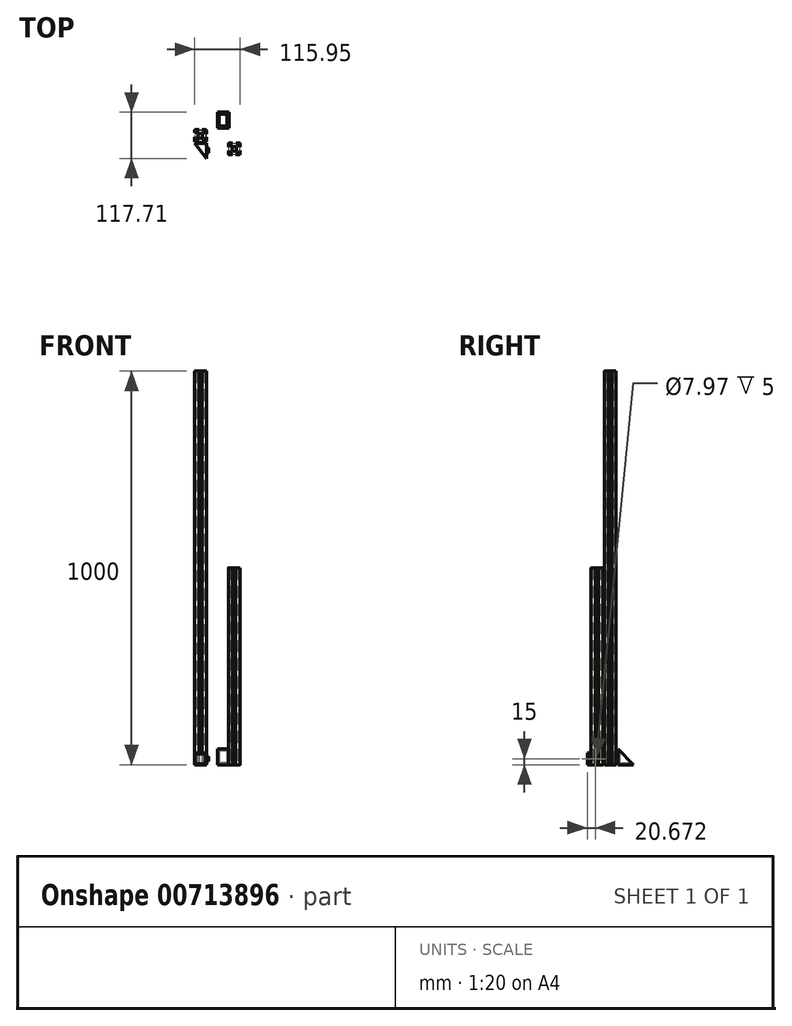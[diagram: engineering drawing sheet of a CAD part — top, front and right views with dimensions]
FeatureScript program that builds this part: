
annotation { "Feature Type Name" : "Feature", "Feature Type Description" : "" }
export const myFeature = defineFeature(function(context is Context, id is Id, definition is map)
    precondition{}
    {
        {
            var Q0;
            Q0=qCreatedBy(makeId("Top.planeOp"),FACE);
            var sketch = newSketch(context, id + "F0", { "sketchPlane" : qUnion([Q0])});
            skPoint(sketch, "E0.middle", {"position": v(-42.85, -16.21) * mm});
            skLineSegment(sketch, "E1.bottom", {"start": v(-36.85, -22.2) * mm, "end": v(-48.85, -22.2) * mm});
            skLineSegment(sketch, "E1.top", {"start": v(-36.85, -10.21) * mm, "end": v(-48.85, -10.21) * mm});
            skLineSegment(sketch, "E1.left", {"start": v(-36.85, -22.2) * mm, "end": v(-36.85, -10.21) * mm});
            skLineSegment(sketch, "E1.right", {"start": v(-48.85, -22.2) * mm, "end": v(-48.85, -10.21) * mm});
            skLineSegment(sketch, "E2.bottom", {"start": v(-51.1, -1.2) * mm, "end": v(-55.85, -1.2) * mm});
            skLineSegment(sketch, "E2.top", {"start": v(-51.1, -7.95) * mm, "end": v(-57.85, -7.95) * mm});
            skLineSegment(sketch, "E2.left", {"start": v(-51.1, -1.2) * mm, "end": v(-51.1, -7.95) * mm});
            skLineSegment(sketch, "E2.right", {"start": v(-57.85, -3.2) * mm, "end": v(-57.85, -7.95) * mm});
            skPoint(sketch, "E2.middle", {"position": v(-54.47, -4.58) * mm});
            skLineSegment(sketch, "E3", {"start": v(-51.1, -1.2) * mm, "end": v(-46.85, -1.2) * mm});
            skLineSegment(sketch, "E4", {"start": v(-46.85, -1.2) * mm, "end": v(-46.85, -3.2) * mm});
            skLineSegment(sketch, "E5", {"start": v(-46.85, -3.2) * mm, "end": v(-51.1, -3.2) * mm});
            skLineSegment(sketch, "E6.bottom", {"start": v(-57.85, -7.95) * mm, "end": v(-55.85, -7.95) * mm});
            skLineSegment(sketch, "E6.top", {"start": v(-57.85, -12.2) * mm, "end": v(-55.85, -12.2) * mm});
            skLineSegment(sketch, "E6.left", {"start": v(-57.85, -7.95) * mm, "end": v(-57.85, -12.2) * mm});
            skLineSegment(sketch, "E6.right", {"start": v(-55.85, -7.95) * mm, "end": v(-55.85, -12.2) * mm});
            skPoint(sketch, "E7", {"position": v(-57.85, -7.95) * mm});
            skPoint(sketch, "E8.visualSharp", {"position": v(-57.85, -1.2) * mm});
            skArc(sketch, "E8.filletArc", {"start": v(-55.85, -1.2) * mm, "mid": v(-57.26, -1.79) * mm, "end": v(-57.85, -3.2) * mm});
            skLineSegment(sketch, "E9", {"start": v(-51.1, -6.76) * mm, "end": v(-47.77, -10.21) * mm});
            skLineSegment(sketch, "E10", {"start": v(-47.77, -10.21) * mm, "end": v(-49.3, -8.63) * mm});
            skLineSegment(sketch, "E11", {"start": v(-52.34, -7.95) * mm, "end": v(-48.85, -11.52) * mm});
            skLineSegment(sketch, "E12.1.0.0", {"start": v(-27.8, -12.2) * mm, "end": v(-29.8, -12.2) * mm});
            skPoint(sketch, "E12.1.0.1", {"position": v(-34.55, -1.2) * mm});
            skLineSegment(sketch, "E12.1.0.2", {"start": v(-27.8, -7.95) * mm, "end": v(-34.55, -7.95) * mm});
            skLineSegment(sketch, "E12.1.0.3", {"start": v(-27.8, -7.95) * mm, "end": v(-27.8, -12.2) * mm});
            skArc(sketch, "E12.1.0.4", {"start": v(-27.8, -3.2) * mm, "mid": v(-28.39, -1.79) * mm, "end": v(-29.8, -1.2) * mm});
            skPoint(sketch, "E12.1.0.5", {"position": v(-27.8, -1.2) * mm});
            skPoint(sketch, "E12.1.0.6", {"position": v(-31.18, -4.57) * mm});
            skLineSegment(sketch, "E12.1.0.7", {"start": v(-34.55, -1.2) * mm, "end": v(-34.55, -3.2) * mm});
            skLineSegment(sketch, "E12.1.0.8", {"start": v(-33.29, -7.95) * mm, "end": v(-36.85, -11.37) * mm});
            skLineSegment(sketch, "E12.1.0.9", {"start": v(-29.8, -12.2) * mm, "end": v(-29.8, -7.95) * mm});
            skLineSegment(sketch, "E12.1.0.10", {"start": v(-29.8, -1.2) * mm, "end": v(-34.55, -1.2) * mm});
            skLineSegment(sketch, "E12.1.0.11", {"start": v(-34.55, -7.95) * mm, "end": v(-34.55, -1.2) * mm});
            skLineSegment(sketch, "E12.1.0.12", {"start": v(-27.8, -7.95) * mm, "end": v(-27.8, -3.2) * mm});
            skLineSegment(sketch, "E12.1.0.13", {"start": v(-34.55, -6.7) * mm, "end": v(-38.14, -10.21) * mm});
            skLineSegment(sketch, "E12.1.0.15", {"start": v(-34.55, -3.2) * mm, "end": v(-38.8, -3.2) * mm});
            skLineSegment(sketch, "E12.1.0.16", {"start": v(-34.55, -1.2) * mm, "end": v(-38.8, -1.2) * mm});
            skLineSegment(sketch, "E12.1.0.17", {"start": v(-38.8, -1.2) * mm, "end": v(-38.8, -3.2) * mm});
            skPoint(sketch, "E13.1.0.0", {"position": v(-27.86, -24.46) * mm});
            skLineSegment(sketch, "E13.1.0.1", {"start": v(-27.86, -29.2) * mm, "end": v(-27.86, -24.46) * mm});
            skLineSegment(sketch, "E13.1.0.2", {"start": v(-27.86, -20.2) * mm, "end": v(-29.86, -20.2) * mm});
            skLineSegment(sketch, "E13.1.0.3", {"start": v(-27.86, -24.46) * mm, "end": v(-27.86, -20.2) * mm});
            skLineSegment(sketch, "E13.1.0.4", {"start": v(-27.86, -24.46) * mm, "end": v(-29.86, -24.46) * mm});
            skLineSegment(sketch, "E13.1.0.5", {"start": v(-34.6, -31.2) * mm, "end": v(-34.6, -24.46) * mm});
            skLineSegment(sketch, "E13.1.0.6", {"start": v(-33.36, -24.46) * mm, "end": v(-36.85, -20.89) * mm});
            skPoint(sketch, "E13.1.0.7", {"position": v(-27.86, -31.2) * mm});
            skLineSegment(sketch, "E13.1.0.8", {"start": v(-34.6, -24.46) * mm, "end": v(-27.86, -24.46) * mm});
            skPoint(sketch, "E13.1.0.9", {"position": v(-31.23, -27.83) * mm});
            skLineSegment(sketch, "E13.1.0.10", {"start": v(-34.6, -31.2) * mm, "end": v(-29.86, -31.2) * mm});
            skLineSegment(sketch, "E13.1.0.11", {"start": v(-29.86, -24.46) * mm, "end": v(-29.86, -20.2) * mm});
            skArc(sketch, "E13.1.0.12", {"start": v(-29.86, -31.2) * mm, "mid": v(-28.44, -30.62) * mm, "end": v(-27.86, -29.2) * mm});
            skLineSegment(sketch, "E13.1.0.13", {"start": v(-34.6, -25.65) * mm, "end": v(-37.93, -22.2) * mm});
            skLineSegment(sketch, "E13.1.0.14", {"start": v(-38.86, -29.2) * mm, "end": v(-34.6, -29.2) * mm});
            skLineSegment(sketch, "E13.1.0.15", {"start": v(-34.6, -31.2) * mm, "end": v(-38.86, -31.2) * mm});
            skLineSegment(sketch, "E13.1.0.16", {"start": v(-38.86, -31.2) * mm, "end": v(-38.86, -29.2) * mm});
            skPoint(sketch, "E14.1.0.0", {"position": v(-51.08, -31.19) * mm});
            skLineSegment(sketch, "E14.1.0.1", {"start": v(-55.83, -31.19) * mm, "end": v(-51.08, -31.19) * mm});
            skLineSegment(sketch, "E14.1.0.2", {"start": v(-46.83, -31.19) * mm, "end": v(-46.83, -29.19) * mm});
            skLineSegment(sketch, "E14.1.0.3", {"start": v(-51.08, -31.19) * mm, "end": v(-46.83, -31.19) * mm});
            skLineSegment(sketch, "E14.1.0.4", {"start": v(-51.08, -31.19) * mm, "end": v(-51.08, -29.19) * mm});
            skLineSegment(sketch, "E14.1.0.5", {"start": v(-57.83, -24.44) * mm, "end": v(-51.08, -24.44) * mm});
            skLineSegment(sketch, "E14.1.0.6", {"start": v(-51.08, -25.68) * mm, "end": v(-47.51, -22.2) * mm});
            skPoint(sketch, "E14.1.0.7", {"position": v(-57.83, -31.19) * mm});
            skLineSegment(sketch, "E14.1.0.8", {"start": v(-51.08, -24.44) * mm, "end": v(-51.08, -31.19) * mm});
            skPoint(sketch, "E14.1.0.9", {"position": v(-54.45, -27.81) * mm});
            skLineSegment(sketch, "E14.1.0.10", {"start": v(-57.83, -24.44) * mm, "end": v(-57.83, -29.19) * mm});
            skLineSegment(sketch, "E14.1.0.11", {"start": v(-51.08, -29.19) * mm, "end": v(-46.83, -29.19) * mm});
            skArc(sketch, "E14.1.0.12", {"start": v(-57.83, -29.19) * mm, "mid": v(-57.24, -30.6) * mm, "end": v(-55.83, -31.19) * mm});
            skLineSegment(sketch, "E14.1.0.13", {"start": v(-52.28, -24.44) * mm, "end": v(-48.82, -21.12) * mm});
            skLineSegment(sketch, "E14.1.0.14", {"start": v(-55.83, -20.19) * mm, "end": v(-55.83, -24.44) * mm});
            skLineSegment(sketch, "E14.1.0.15", {"start": v(-57.83, -24.44) * mm, "end": v(-57.83, -20.19) * mm});
            skLineSegment(sketch, "E14.1.0.16", {"start": v(-57.83, -20.19) * mm, "end": v(-55.83, -20.19) * mm});
            skSolve(sketch);
        }
        {
            var Q0;
            {var subQ1=sQuery(id+"F0.wireOp",EDGE,"E1.bottom");var subQ4=sQuery(id+"F0.wireOp",EDGE,"E1.left");var subQ9=makeQuery(id+"F0.imprint","INTERSECT",VERTEX,{"derivedFrom":[subQ1,subQ4]});Q0=makeQuery(id+"F0.imprint","IMPRINT",FACE,{"disambiguationData":[TD([[makeQuery(id+"F0.imprint","IMPRINT",EDGE,{"disambiguationData":[TD([[subQ9,-1.0]])],"derivedFrom":subQ1}),-1.0]])]});}
            var Q1;
            {var subQ6=sQuery(id+"F0.wireOp",EDGE,"E14.1.0.1");Q1=makeQuery(id+"F0.imprint","IMPRINT",FACE,{"disambiguationData":[TD([[makeQuery(id+"F0.imprint","IMPRINT",EDGE,{"derivedFrom":subQ6}),1.0]])]});}
            var Q2;
            Q2=makeQuery(id+"F0.imprint","IMPRINT",FACE,{"disambiguationData":[TD([[makeQuery(id+"F0.imprint","IMPRINT",EDGE,{"derivedFrom":sQuery(id+"F0.wireOp",EDGE,"E12.1.0.4")}),1.0]])]});
            var Q3;
            {var subQ6=sQuery(id+"F0.wireOp",EDGE,"E13.1.0.1");Q3=makeQuery(id+"F0.imprint","IMPRINT",FACE,{"disambiguationData":[TD([[makeQuery(id+"F0.imprint","IMPRINT",EDGE,{"derivedFrom":subQ6}),1.0]])]});}
            var Q4;
            {var subQ1=sQuery(id+"F0.wireOp",EDGE,"E2.bottom");Q4=makeQuery(id+"F0.imprint","IMPRINT",FACE,{"disambiguationData":[TD([[makeQuery(id+"F0.imprint","IMPRINT",EDGE,{"derivedFrom":subQ1}),1.0]])]});}
            var Q5;
            {var subQ0=sQuery(id+"F0.wireOp",EDGE,"E3");Q5=makeQuery(id+"F0.imprint","IMPRINT",FACE,{"disambiguationData":[TD([[makeQuery(id+"F0.imprint","IMPRINT",EDGE,{"derivedFrom":subQ0}),-1.0]])]});}
            var Q6;
            Q6=makeQuery(id+"F0.imprint","IMPRINT",FACE,{"disambiguationData":[TD([[makeQuery(id+"F0.imprint","IMPRINT",EDGE,{"derivedFrom":sQuery(id+"F0.wireOp",EDGE,"E6.bottom")}),-1.0]])]});
            var Q7;
            Q7=makeQuery(id+"F0.imprint","IMPRINT",FACE,{"disambiguationData":[TD([[makeQuery(id+"F0.imprint","IMPRINT",EDGE,{"derivedFrom":sQuery(id+"F0.wireOp",EDGE,"E12.1.0.0")}),-1.0]])]});
            var Q8;
            Q8=makeQuery(id+"F0.imprint","IMPRINT",FACE,{"disambiguationData":[TD([[makeQuery(id+"F0.imprint","IMPRINT",EDGE,{"derivedFrom":sQuery(id+"F0.wireOp",EDGE,"E13.1.0.2")}),1.0]])]});
            var Q9;
            Q9=makeQuery(id+"F0.imprint","IMPRINT",FACE,{"disambiguationData":[TD([[makeQuery(id+"F0.imprint","IMPRINT",EDGE,{"derivedFrom":sQuery(id+"F0.wireOp",EDGE,"E14.1.0.2")}),1.0]])]});
            var Q10;
            {var subQ2=sQuery(id+"F0.wireOp",EDGE,"E14.1.0.14");Q10=makeQuery(id+"F0.imprint","IMPRINT",FACE,{"disambiguationData":[TD([[makeQuery(id+"F0.imprint","IMPRINT",EDGE,{"derivedFrom":subQ2}),-1.0]])]});}
            var Q11;
            {var subQ0=sQuery(id+"F0.wireOp",EDGE,"E13.1.0.6");Q11=makeQuery(id+"F0.imprint","IMPRINT",FACE,{"disambiguationData":[TD([[makeQuery(id+"F0.imprint","IMPRINT",EDGE,{"derivedFrom":subQ0}),1.0]])]});}
            var Q12;
            {var subQ3=sQuery(id+"F0.wireOp",EDGE,"E1.bottom");var subQ9=sQuery(id+"F0.wireOp",EDGE,"E1.right");var subQ10=makeQuery(id+"F0.imprint","INTERSECT",VERTEX,{"derivedFrom":[subQ3,subQ9]});Q12=makeQuery(id+"F0.imprint","IMPRINT",FACE,{"disambiguationData":[TD([[makeQuery(id+"F0.imprint","IMPRINT",EDGE,{"disambiguationData":[TD([[subQ10,1.0]])],"derivedFrom":subQ3}),1.0]])]});}
            var Q13;
            {var subQ0=sQuery(id+"F0.wireOp",EDGE,"E12.1.0.8");Q13=makeQuery(id+"F0.imprint","IMPRINT",FACE,{"disambiguationData":[TD([[makeQuery(id+"F0.imprint","IMPRINT",EDGE,{"derivedFrom":subQ0}),-1.0]])]});}
            var Q14;
            {var subQ3=sQuery(id+"F0.wireOp",EDGE,"E9");Q14=makeQuery(id+"F0.imprint","IMPRINT",FACE,{"disambiguationData":[TD([[makeQuery(id+"F0.imprint","IMPRINT",EDGE,{"derivedFrom":subQ3}),-1.0]])]});}
            var Q15;
            {var subQ2=sQuery(id+"F0.wireOp",EDGE,"E12.1.0.15");Q15=makeQuery(id+"F0.imprint","IMPRINT",FACE,{"disambiguationData":[TD([[makeQuery(id+"F0.imprint","IMPRINT",EDGE,{"derivedFrom":subQ2}),-1.0]])]});}
            var Q16;
            {var subQ2=sQuery(id+"F0.wireOp",EDGE,"E13.1.0.14");Q16=makeQuery(id+"F0.imprint","IMPRINT",FACE,{"disambiguationData":[TD([[makeQuery(id+"F0.imprint","IMPRINT",EDGE,{"derivedFrom":subQ2}),-1.0]])]});}
            extrude(context, id + "F1", {"entities" : qUnion([Q0, Q1, Q2, Q3, Q4, Q5, Q6, Q7, Q8, Q9, Q10, Q11, Q12, Q13, Q14, Q15, Q16]), "depth" : 1000 * mm, "offsetDistance" : 25 * mm});
        }
        {
            var Q0;
            Q0=qCreatedBy(makeId("Top.planeOp"),FACE);
            var sketch = newSketch(context, id + "F2", { "sketchPlane" : qUnion([Q0])});
            skPoint(sketch, "E15.middle", {"position": v(42.98, -49.46) * mm});
            skLineSegment(sketch, "E16.bottom", {"start": v(48.98, -55.46) * mm, "end": v(36.98, -55.46) * mm});
            skLineSegment(sketch, "E16.top", {"start": v(48.98, -43.46) * mm, "end": v(36.98, -43.46) * mm});
            skLineSegment(sketch, "E16.left", {"start": v(48.98, -55.46) * mm, "end": v(48.98, -43.46) * mm});
            skLineSegment(sketch, "E16.right", {"start": v(36.98, -55.46) * mm, "end": v(36.98, -43.46) * mm});
            skLineSegment(sketch, "E17.bottom", {"start": v(34.73, -34.45) * mm, "end": v(29.98, -34.45) * mm});
            skLineSegment(sketch, "E17.top", {"start": v(34.73, -41.2) * mm, "end": v(27.98, -41.2) * mm});
            skLineSegment(sketch, "E17.left", {"start": v(34.73, -34.45) * mm, "end": v(34.73, -41.2) * mm});
            skLineSegment(sketch, "E17.right", {"start": v(27.98, -36.45) * mm, "end": v(27.98, -41.2) * mm});
            skPoint(sketch, "E17.middle", {"position": v(31.35, -37.83) * mm});
            skLineSegment(sketch, "E18", {"start": v(34.73, -34.45) * mm, "end": v(38.98, -34.45) * mm});
            skLineSegment(sketch, "E19", {"start": v(38.98, -34.45) * mm, "end": v(38.98, -36.45) * mm});
            skLineSegment(sketch, "E20", {"start": v(38.98, -36.45) * mm, "end": v(34.73, -36.45) * mm});
            skLineSegment(sketch, "E21.bottom", {"start": v(27.98, -41.2) * mm, "end": v(29.98, -41.2) * mm});
            skLineSegment(sketch, "E21.top", {"start": v(27.98, -45.45) * mm, "end": v(29.98, -45.45) * mm});
            skLineSegment(sketch, "E21.left", {"start": v(27.98, -41.2) * mm, "end": v(27.98, -45.45) * mm});
            skLineSegment(sketch, "E21.right", {"start": v(29.98, -41.2) * mm, "end": v(29.98, -45.45) * mm});
            skPoint(sketch, "E22", {"position": v(27.98, -41.2) * mm});
            skPoint(sketch, "E23.visualSharp", {"position": v(27.98, -34.45) * mm});
            skArc(sketch, "E23.filletArc", {"start": v(29.98, -34.45) * mm, "mid": v(28.57, -35.04) * mm, "end": v(27.98, -36.45) * mm});
            skLineSegment(sketch, "E24", {"start": v(34.73, -40) * mm, "end": v(38.06, -43.46) * mm});
            skLineSegment(sketch, "E25", {"start": v(38.06, -43.46) * mm, "end": v(36.53, -41.88) * mm});
            skLineSegment(sketch, "E26", {"start": v(33.49, -41.2) * mm, "end": v(36.98, -44.77) * mm});
            skLineSegment(sketch, "E27.1.0.0", {"start": v(58.03, -45.45) * mm, "end": v(56.03, -45.45) * mm});
            skPoint(sketch, "E27.1.0.1", {"position": v(51.28, -34.45) * mm});
            skLineSegment(sketch, "E27.1.0.2", {"start": v(58.03, -41.2) * mm, "end": v(51.28, -41.2) * mm});
            skLineSegment(sketch, "E27.1.0.3", {"start": v(58.03, -41.2) * mm, "end": v(58.03, -45.45) * mm});
            skArc(sketch, "E27.1.0.4", {"start": v(58.03, -36.45) * mm, "mid": v(57.44, -35.04) * mm, "end": v(56.03, -34.45) * mm});
            skPoint(sketch, "E27.1.0.5", {"position": v(58.03, -34.45) * mm});
            skPoint(sketch, "E27.1.0.6", {"position": v(54.65, -37.82) * mm});
            skLineSegment(sketch, "E27.1.0.7", {"start": v(51.28, -34.45) * mm, "end": v(51.28, -36.45) * mm});
            skLineSegment(sketch, "E27.1.0.8", {"start": v(52.54, -41.2) * mm, "end": v(48.98, -44.62) * mm});
            skLineSegment(sketch, "E27.1.0.9", {"start": v(56.03, -45.45) * mm, "end": v(56.03, -41.2) * mm});
            skLineSegment(sketch, "E27.1.0.10", {"start": v(56.03, -34.45) * mm, "end": v(51.28, -34.45) * mm});
            skLineSegment(sketch, "E27.1.0.11", {"start": v(51.28, -41.2) * mm, "end": v(51.28, -34.45) * mm});
            skLineSegment(sketch, "E27.1.0.12", {"start": v(58.03, -41.2) * mm, "end": v(58.03, -36.45) * mm});
            skLineSegment(sketch, "E27.1.0.13", {"start": v(51.28, -39.96) * mm, "end": v(47.7, -43.46) * mm});
            skLineSegment(sketch, "E27.1.0.15", {"start": v(51.28, -36.45) * mm, "end": v(47.03, -36.45) * mm});
            skLineSegment(sketch, "E27.1.0.16", {"start": v(51.28, -34.45) * mm, "end": v(47.03, -34.45) * mm});
            skLineSegment(sketch, "E27.1.0.17", {"start": v(47.03, -34.45) * mm, "end": v(47.03, -36.45) * mm});
            skPoint(sketch, "E28.1.0.0", {"position": v(57.97, -57.7) * mm});
            skLineSegment(sketch, "E28.1.0.1", {"start": v(57.97, -62.46) * mm, "end": v(57.97, -57.7) * mm});
            skLineSegment(sketch, "E28.1.0.2", {"start": v(57.97, -53.46) * mm, "end": v(55.97, -53.46) * mm});
            skLineSegment(sketch, "E28.1.0.3", {"start": v(57.97, -57.7) * mm, "end": v(57.97, -53.46) * mm});
            skLineSegment(sketch, "E28.1.0.4", {"start": v(57.97, -57.7) * mm, "end": v(55.97, -57.7) * mm});
            skLineSegment(sketch, "E28.1.0.5", {"start": v(51.22, -64.46) * mm, "end": v(51.22, -57.7) * mm});
            skLineSegment(sketch, "E28.1.0.6", {"start": v(52.47, -57.7) * mm, "end": v(48.98, -54.14) * mm});
            skPoint(sketch, "E28.1.0.7", {"position": v(57.97, -64.46) * mm});
            skLineSegment(sketch, "E28.1.0.8", {"start": v(51.22, -57.7) * mm, "end": v(57.97, -57.7) * mm});
            skPoint(sketch, "E28.1.0.9", {"position": v(54.6, -61.08) * mm});
            skLineSegment(sketch, "E28.1.0.10", {"start": v(51.22, -64.46) * mm, "end": v(55.97, -64.46) * mm});
            skLineSegment(sketch, "E28.1.0.11", {"start": v(55.97, -57.7) * mm, "end": v(55.97, -53.46) * mm});
            skArc(sketch, "E28.1.0.12", {"start": v(55.97, -64.46) * mm, "mid": v(57.39, -63.87) * mm, "end": v(57.97, -62.46) * mm});
            skLineSegment(sketch, "E28.1.0.13", {"start": v(51.22, -58.9) * mm, "end": v(47.9, -55.45) * mm});
            skLineSegment(sketch, "E28.1.0.14", {"start": v(46.97, -62.46) * mm, "end": v(51.22, -62.46) * mm});
            skLineSegment(sketch, "E28.1.0.15", {"start": v(51.22, -64.46) * mm, "end": v(46.97, -64.46) * mm});
            skLineSegment(sketch, "E28.1.0.16", {"start": v(46.97, -64.46) * mm, "end": v(46.97, -62.46) * mm});
            skPoint(sketch, "E29.1.0.0", {"position": v(34.75, -64.44) * mm});
            skLineSegment(sketch, "E29.1.0.1", {"start": v(30, -64.44) * mm, "end": v(34.75, -64.44) * mm});
            skLineSegment(sketch, "E29.1.0.2", {"start": v(39, -64.44) * mm, "end": v(39, -62.44) * mm});
            skLineSegment(sketch, "E29.1.0.3", {"start": v(34.75, -64.44) * mm, "end": v(39, -64.44) * mm});
            skLineSegment(sketch, "E29.1.0.4", {"start": v(34.75, -64.44) * mm, "end": v(34.75, -62.44) * mm});
            skLineSegment(sketch, "E29.1.0.5", {"start": v(28, -57.69) * mm, "end": v(34.75, -57.69) * mm});
            skLineSegment(sketch, "E29.1.0.6", {"start": v(34.75, -58.93) * mm, "end": v(38.32, -55.44) * mm});
            skPoint(sketch, "E29.1.0.7", {"position": v(28, -64.44) * mm});
            skLineSegment(sketch, "E29.1.0.8", {"start": v(34.75, -57.69) * mm, "end": v(34.75, -64.44) * mm});
            skPoint(sketch, "E29.1.0.9", {"position": v(31.38, -61.06) * mm});
            skLineSegment(sketch, "E29.1.0.10", {"start": v(28, -57.69) * mm, "end": v(28, -62.44) * mm});
            skLineSegment(sketch, "E29.1.0.11", {"start": v(34.75, -62.44) * mm, "end": v(39, -62.44) * mm});
            skArc(sketch, "E29.1.0.12", {"start": v(28, -62.44) * mm, "mid": v(28.59, -63.85) * mm, "end": v(30, -64.44) * mm});
            skLineSegment(sketch, "E29.1.0.13", {"start": v(33.55, -57.69) * mm, "end": v(37, -54.37) * mm});
            skLineSegment(sketch, "E29.1.0.14", {"start": v(30, -53.44) * mm, "end": v(30, -57.69) * mm});
            skLineSegment(sketch, "E29.1.0.15", {"start": v(28, -57.69) * mm, "end": v(28, -53.44) * mm});
            skLineSegment(sketch, "E29.1.0.16", {"start": v(28, -53.44) * mm, "end": v(30, -53.44) * mm});
            skSolve(sketch);
        }
        {
            var Q0;
            Q0 = qSketchRegion(id + "F2", true);
            extrude(context, id + "F3", {"entities" : qUnion([Q0]), "depth" : 500 * mm, "offsetDistance" : 25 * mm});
        }
        {
            var Q0;
            Q0=qCreatedBy(makeId("Right.planeOp"),FACE);
            var sketch = newSketch(context, id + "F4", { "sketchPlane" : qUnion([Q0])});
            skLineSegment(sketch, "E30", {"start": v(3.3, 0) * mm, "end": v(43.42, 0) * mm});
            skLineSegment(sketch, "E31", {"start": v(3.3, 0) * mm, "end": v(3.3, 40.11) * mm});
            skLineSegment(sketch, "E32", {"start": v(3.3, 40.11) * mm, "end": v(43.42, 0) * mm});
            skSolve(sketch);
        }
        {
            var Q0;
            Q0=makeQuery(id+"F4.imprint","IMPRINT",FACE,{"disambiguationData":[TD([[makeQuery(id+"F4.imprint","IMPRINT",EDGE,{"derivedFrom":sQuery(id+"F4.wireOp",EDGE,"E30")}),1.0]])]});
            extrude(context, id + "F5", {"entities" : qUnion([Q0]), "depth" : 30 * mm, "offsetDistance" : 25 * mm});
        }
        {
            var Q0;
            Q0=makeQuery(id+"F5.opExtrude","SWEPT_FACE",FACE,{"disambiguationData":[OSD([sQuery(id+"F4.wireOp",EDGE,"E32")])]});
            shell(context, id + "F6", {"entities" : qUnion([Q0]), "thickness" : 5 * mm});
        }
        {
            var Q0;
            Q0=qCreatedBy(makeId("Top.planeOp"),FACE);
            var sketch = newSketch(context, id + "F7", { "sketchPlane" : qUnion([Q0])});
            skLineSegment(sketch, "E33", {"start": v(-57.92, -34.99) * mm, "end": v(-27.24, -34.99) * mm});
            skLineSegment(sketch, "E34", {"start": v(-27.24, -34.99) * mm, "end": v(-27.24, -74.3) * mm});
            skLineSegment(sketch, "E35", {"start": v(-27.24, -74.3) * mm, "end": v(-57.92, -34.99) * mm});
            skSolve(sketch);
        }
        {
            var Q0;
            Q0=makeQuery(id+"F7.imprint","IMPRINT",FACE,{"disambiguationData":[TD([[makeQuery(id+"F7.imprint","IMPRINT",EDGE,{"derivedFrom":sQuery(id+"F7.wireOp",EDGE,"E33")}),-1.0]])]});
            extrude(context, id + "F8", {"entities" : qUnion([Q0]), "depth" : 30 * mm, "offsetDistance" : 25 * mm});
        }
        {
            var Q0;
            Q0=makeQuery(id+"F8.opExtrude","SWEPT_FACE",FACE,{"disambiguationData":[OSD([sQuery(id+"F7.wireOp",EDGE,"E35")])]});
            shell(context, id + "F9", {"entities" : qUnion([Q0]), "thickness" : 2.5 * mm});
        }
        {
            var Q0;
            Q0=makeQuery(id+"F8.opExtrude","SWEPT_FACE",FACE,{"disambiguationData":[OSD([sQuery(id+"F7.wireOp",EDGE,"E34")])]});
            var sketch = newSketch(context, id + "F10", { "sketchPlane" : qUnion([Q0])});
            skCircle(sketch, "E36", {"center": v(-53.62, 15) * mm, "radius": 3.99 * mm});
            skPoint(sketch, "E36.centerSnap0", {"position": v(-74.3, 15) * mm});
            skCircle(sketch, "E37", {"center": v(-53.62, 15) * mm, "radius": 6.74 * mm});
            skSolve(sketch);
        }
        {
            var Q0;
            Q0=makeQuery(id+"F10.imprint","IMPRINT",FACE,{"disambiguationData":[TD([[makeQuery(id+"F10.imprint","IMPRINT",EDGE,{"derivedFrom":sQuery(id+"F10.wireOp",EDGE,"E36")}),-1.0]])]});
            extrude(context, id + "F11", {"entities" : qUnion([Q0]), "operationType" : NewBodyOperationType.ADD, "depth" : 5 * mm, "offsetDistance" : 25 * mm});
        }
    });
